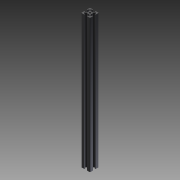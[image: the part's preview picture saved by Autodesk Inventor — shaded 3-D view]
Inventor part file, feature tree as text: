
AUTODESK INVENTOR PART (.ipt)
format: ipt  version: 2014 SP1 (Build 180222100, 222)  size: 172,032 bytes
history: native  units: mm
features: other x7, sketch x2, extrude x1, revolve x1
ambient origin geometry x8: Origin, YZ Plane, XZ Plane, XY Plane, X Axis, Y Axis, Z Axis, Center Point
bodies: Solid1 (feature_tree)
feature tree (11):
  extrude  "Extrusion1"  TaperAngle=360.0deg  [1 undecoded]
  revolve  "Revolution1"  [1 undecoded]
  other  "C1_XY"
  other  "C1_YZ"
  other  "C1_ZX"
  other  "C1_X"
  other  "C1_Y"
  other  "C1_Z"
  other  "C1_Center"
  sketch  "Sketch_1"  dims[d0=306.0mm d1=0.0mm d2=360.0deg]
  sketch  "Sketch_2"
note: 2 required parameter values undecoded (feature->parameter linkage not recoverable at this tier; creation-order binding heuristic only, values carry confidence <= 0.55)
